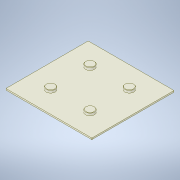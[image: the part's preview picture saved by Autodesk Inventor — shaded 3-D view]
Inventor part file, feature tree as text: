
AUTODESK INVENTOR PART (.ipt)
format: ipt  version: 2022 (Build 260153000, 153)  size: 182,272 bytes
history: native  units: in
note: dims shown in document units (in); Inventor stores cm internally (conversion verified against a paired STEP export)
features: extrude x3, fillet x3, sketch x3
ambient origin geometry x8: Origin, YZ Plane, XZ Plane, XY Plane, X Axis, Y Axis, Z Axis, Center Point
bodies: Solid1 (feature_tree)
feature tree (9):
  extrude  "Extrusion1"  Depth=1.8898in
  extrude  "Extrusion2"  Depth=0.0079in
  fillet  "Fillet1"  Radius=0.0591in
  fillet  "Fillet2"  Radius=0.0079in
  extrude  "Extrusion3"  Depth=1.7264in
  fillet  "Fillet3"  Radius=1.6772in
  sketch  "Sketch1"  dims[d0=1.811in d1=1.8898in]
  sketch  "Sketch2"  dims[d2=0.0787in d3=0.0in d4=0.1969in d8=0.0591in d9=0.0in d10=0.0079in]
  sketch  "Sketch3"  dims[d11=0.0079in d12=1.7264in d13=1.6772in d14=0.0394in d15=0.0in d16=0.0079in d17=0.4331in d18=0.4331in d19=0.7874in d21=0.8661in d22=0.7874in d24=0.8661in]
